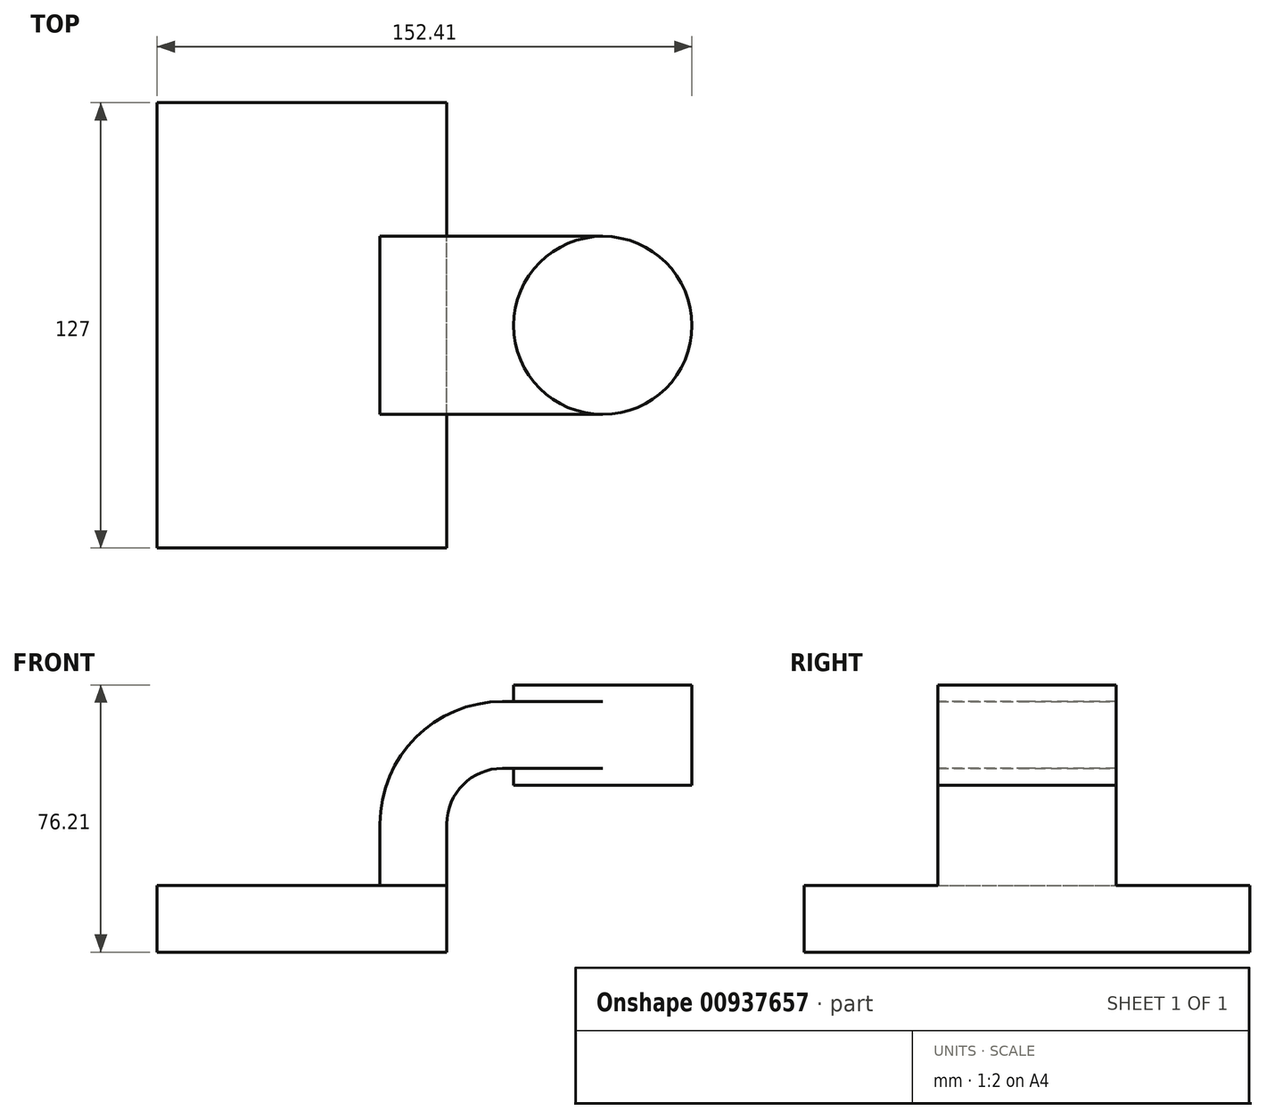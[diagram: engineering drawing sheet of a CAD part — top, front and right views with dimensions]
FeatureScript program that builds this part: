
annotation { "Feature Type Name" : "Feature", "Feature Type Description" : "" }
export const myFeature = defineFeature(function(context is Context, id is Id, definition is map)
    precondition{}
    {
        {
            var Q0;
            Q0=qCreatedBy(makeId("Front.planeOp"),FACE);
            var sketch = newSketch(context, id + "F0", { "sketchPlane" : qUnion([Q0])});
            skLineSegment(sketch, "E0.bottom", {"start": v(41.28, -9.52) * mm, "end": v(-41.27, -9.53) * mm});
            skLineSegment(sketch, "E0.top", {"start": v(41.27, 9.53) * mm, "end": v(-41.28, 9.53) * mm});
            skLineSegment(sketch, "E0.left", {"start": v(41.28, -9.52) * mm, "end": v(41.28, 9.53) * mm});
            skLineSegment(sketch, "E0.right", {"start": v(-41.27, -9.52) * mm, "end": v(-41.28, 9.53) * mm});
            skPoint(sketch, "E0.middle", {"position": v(0, 0) * mm});
            skLineSegment(sketch, "E1.bottom", {"start": v(111.12, 38.1) * mm, "end": v(60.33, 38.1) * mm});
            skLineSegment(sketch, "E1.top", {"start": v(111.12, 66.68) * mm, "end": v(60.33, 66.68) * mm});
            skLineSegment(sketch, "E1.left", {"start": v(111.12, 38.1) * mm, "end": v(111.12, 66.68) * mm});
            skLineSegment(sketch, "E1.right", {"start": v(60.33, 38.1) * mm, "end": v(60.33, 66.68) * mm});
            skPoint(sketch, "E1.middle", {"position": v(85.73, 52.39) * mm});
            skLineSegment(sketch, "E2", {"start": v(41.27, 9.53) * mm, "end": v(41.27, 27) * mm});
            skArc(sketch, "E3", {"start": v(41.28, 27) * mm, "mid": v(45.92, 38.23) * mm, "end": v(57.15, 42.88) * mm});
            skLineSegment(sketch, "E4", {"start": v(57.15, 42.88) * mm, "end": v(85.73, 42.88) * mm});
            skLineSegment(sketch, "E5.0", {"start": v(57.15, 61.93) * mm, "end": v(85.73, 61.93) * mm});
            skArc(sketch, "E5.1", {"start": v(22.23, 27) * mm, "mid": v(32.45, 51.7) * mm, "end": v(57.15, 61.93) * mm});
            skLineSegment(sketch, "E5.2", {"start": v(22.23, 9.53) * mm, "end": v(22.23, 27) * mm});
            skLineSegment(sketch, "E6", {"start": v(85.73, 38.1) * mm, "end": v(85.73, 66.68) * mm});
            skFitSpline(sketch, "E7", {"points": [v(-41.28, 9.53) * mm, v(-36.1, 29.43) * mm, v(-27.92, 23.65) * mm, v(-19.73, 37.14) * mm, v(-12.18, 29.92) * mm, v(-2.7, 41) * mm, v(0, 48.06) * mm, v(6.93, 47.74) * mm, v(14.47, 57.53) * mm, v(27.16, 53.68) * mm, v(40.97, 63.48) * mm, v(53.17, 64.6) * mm, v(57.15, 61.93) * mm], "startDerivative": vector(26.7, 281.57) * mm, "endDerivative": vector(59.72, -56.08) * mm});
            skSolve(sketch);
        }
        {
            var Q0;
            Q0=makeQuery(id+"F0.imprint","IMPRINT",FACE,{"disambiguationData":[TD([[makeQuery(id+"F0.imprint","IMPRINT",EDGE,{"derivedFrom":sQuery(id+"F0.wireOp",EDGE,"E0.bottom")}),-1.0]])]});
            extrude(context, id + "F1", {"entities" : qUnion([Q0]), "endBound" : BoundingType.SYMMETRIC, "depth" : 127 * mm, "offsetDistance" : 25.4 * mm});
        }
        {
            var Q0;
            {var subQ1=sQuery(id+"F0.wireOp",EDGE,"E2");Q0=makeQuery(id+"F0.imprint","IMPRINT",FACE,{"disambiguationData":[TD([[makeQuery(id+"F0.imprint","IMPRINT",EDGE,{"derivedFrom":subQ1}),1.0]])]});}
            var Q1;
            {var subQ0=sQuery(id+"F0.wireOp",EDGE,"E4");var subQ1=sQuery(id+"F0.wireOp",EDGE,"E1.right");var subQ2=makeQuery(id+"F0.imprint","INTERSECT",VERTEX,{"derivedFrom":[subQ1,subQ0]});Q1=makeQuery(id+"F0.imprint","IMPRINT",FACE,{"disambiguationData":[TD([[makeQuery(id+"F0.imprint","IMPRINT",EDGE,{"disambiguationData":[TD([[subQ2,-1.0]])],"derivedFrom":subQ1}),-1.0]])]});}
            extrude(context, id + "F2", {"entities" : qUnion([Q0, Q1]), "operationType" : NewBodyOperationType.ADD, "endBound" : BoundingType.SYMMETRIC, "depth" : 50.8 * mm, "offsetDistance" : 25.4 * mm});
        }
        {
            var Q0;
            Q0=makeQuery(id+"F0.imprint","IMPRINT",FACE,{"disambiguationData":[TD([[makeQuery(id+"F0.imprint","IMPRINT",EDGE,{"derivedFrom":sQuery(id+"F0.wireOp",EDGE,"E5.1")}),1.0]])]});
            extrude(context, id + "F3", {"entities" : qUnion([Q0]), "operationType" : NewBodyOperationType.ADD, "endBound" : BoundingType.SYMMETRIC, "depth" : 15.88 * mm, "offsetDistance" : 25.4 * mm});
        }
        {
            var Q0;
            {var subQ4=sQuery(id+"F0.wireOp",EDGE,"E1.left");Q0=makeQuery(id+"F0.imprint","IMPRINT",FACE,{"disambiguationData":[TD([[makeQuery(id+"F0.imprint","IMPRINT",EDGE,{"derivedFrom":subQ4}),1.0]])]});}
            var Q1;
            Q1=sQuery(id+"F0.wireOp",EDGE,"E6");
            revolve(context, id + "F4", {"operationType" : NewBodyOperationType.ADD, "surfaceOperationType" : NewSurfaceOperationType.NEW, "entities" : qUnion([Q0]), "axis" : qUnion([Q1]), "revolveType" : RevolveType.FULL});
        }
    });
